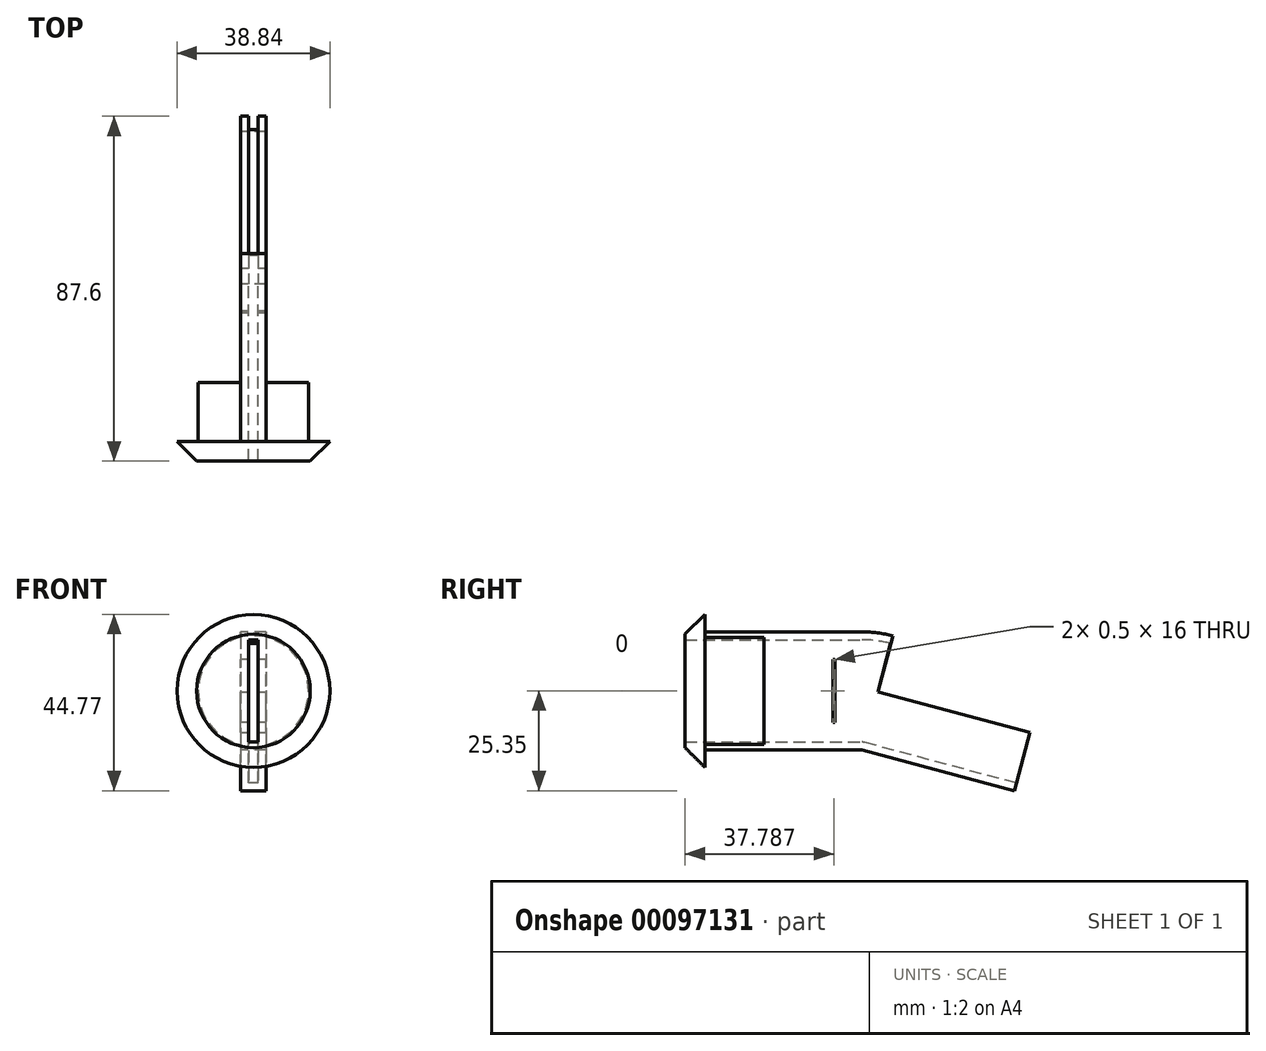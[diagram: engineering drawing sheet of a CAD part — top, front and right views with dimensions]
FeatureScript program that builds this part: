
annotation { "Feature Type Name" : "Feature", "Feature Type Description" : "" }
export const myFeature = defineFeature(function(context is Context, id is Id, definition is map)
    precondition{}
    {
        {
            var Q0;
            Q0=qCreatedBy(makeId("Front.planeOp"),FACE);
            var sketch = newSketch(context, id + "F0", { "sketchPlane" : qUnion([Q0])});
            skCircle(sketch, "E0", {"center": v(0, 0) * mm, "radius": 19.42 * mm});
            skCircle(sketch, "E1", {"center": v(0, 0) * mm, "radius": 14 * mm});
            skLineSegment(sketch, "E2.bottom", {"start": v(1.25, 13) * mm, "end": v(-1.25, 13) * mm});
            skLineSegment(sketch, "E2.top", {"start": v(1.25, -13) * mm, "end": v(-1.25, -13) * mm});
            skLineSegment(sketch, "E2.left", {"start": v(1.25, 13) * mm, "end": v(1.25, -13) * mm});
            skLineSegment(sketch, "E2.right", {"start": v(-1.25, 13) * mm, "end": v(-1.25, -13) * mm});
            skLineSegment(sketch, "E3.0", {"start": v(-3.25, 15) * mm, "end": v(-3.25, -15) * mm});
            skLineSegment(sketch, "E3.1", {"start": v(3.25, 15) * mm, "end": v(-3.25, 15) * mm});
            skLineSegment(sketch, "E3.2", {"start": v(3.25, 15) * mm, "end": v(3.25, -15) * mm});
            skLineSegment(sketch, "E3.3", {"start": v(3.25, -15) * mm, "end": v(-3.25, -15) * mm});
            skSolve(sketch);
        }
        {
            var Q0;
            {var subQ0=sQuery(id+"F0.wireOp",EDGE,"E3.0");var subQ1=sQuery(id+"F0.wireOp",EDGE,"E1");var subQ2=makeQuery(id+"F0.imprint","INTERSECT",VERTEX,{"disambiguationData":[OD(0.0)],"derivedFrom":[subQ1,subQ0]});Q0=makeQuery(id+"F0.imprint","IMPRINT",FACE,{"disambiguationData":[TD([[makeQuery(id+"F0.imprint","IMPRINT",EDGE,{"disambiguationData":[TD([[subQ2,-1.0]])],"derivedFrom":subQ1}),1.0]])]});}
            var Q1;
            Q1=makeQuery(id+"F0.imprint","IMPRINT",FACE,{"disambiguationData":[TD([[makeQuery(id+"F0.imprint","IMPRINT",EDGE,{"derivedFrom":sQuery(id+"F0.wireOp",EDGE,"E0")}),1.0]])]});
            var Q2;
            {var subQ0=sQuery(id+"F0.wireOp",EDGE,"E3.2");var subQ1=sQuery(id+"F0.wireOp",EDGE,"E1");var subQ2=makeQuery(id+"F0.imprint","INTERSECT",VERTEX,{"disambiguationData":[OD(0.0)],"derivedFrom":[subQ1,subQ0]});Q2=makeQuery(id+"F0.imprint","IMPRINT",FACE,{"disambiguationData":[TD([[makeQuery(id+"F0.imprint","IMPRINT",EDGE,{"disambiguationData":[TD([[subQ2,1.0]])],"derivedFrom":subQ1}),1.0]])]});}
            var Q3;
            Q3=makeQuery(id+"F0.imprint","IMPRINT",FACE,{"disambiguationData":[TD([[makeQuery(id+"F0.imprint","IMPRINT",EDGE,{"derivedFrom":sQuery(id+"F0.wireOp",EDGE,"E2.bottom")}),-1.0]])]});
            var Q4;
            {var subQ5=sQuery(id+"F0.wireOp",EDGE,"E3.3");Q4=makeQuery(id+"F0.imprint","IMPRINT",FACE,{"disambiguationData":[TD([[makeQuery(id+"F0.imprint","IMPRINT",EDGE,{"derivedFrom":subQ5}),-1.0]])]});}
            var Q5;
            {var subQ5=sQuery(id+"F0.wireOp",EDGE,"E3.1");Q5=makeQuery(id+"F0.imprint","IMPRINT",FACE,{"disambiguationData":[TD([[makeQuery(id+"F0.imprint","IMPRINT",EDGE,{"derivedFrom":subQ5}),1.0]])]});}
            extrude(context, id + "F1", {"entities" : qUnion([Q0, Q1, Q2, Q3, Q4, Q5]), "depth" : 5 * mm});
        }
        {
            var Q0;
            Q0=makeQuery(id+"F1.opExtrude","CAP_EDGE",EDGE,{"disambiguationData":[OSD([sQuery(id+"F0.wireOp",EDGE,"E0")])],"isStart":false});
            chamfer(context, id + "F2", {"entities" : qUnion([Q0]), "width" : 5 * mm, "tangentPropagation" : true});
        }
        {
            var Q0;
            {var subQ5=sQuery(id+"F0.wireOp",EDGE,"E3.1");Q0=makeQuery(id+"F0.imprint","IMPRINT",FACE,{"disambiguationData":[TD([[makeQuery(id+"F0.imprint","IMPRINT",EDGE,{"derivedFrom":subQ5}),1.0]])]});}
            var Q1;
            Q1=makeQuery(id+"F0.imprint","IMPRINT",FACE,{"disambiguationData":[TD([[makeQuery(id+"F0.imprint","IMPRINT",EDGE,{"derivedFrom":sQuery(id+"F0.wireOp",EDGE,"E2.bottom")}),-1.0]])]});
            var Q2;
            {var subQ5=sQuery(id+"F0.wireOp",EDGE,"E3.3");Q2=makeQuery(id+"F0.imprint","IMPRINT",FACE,{"disambiguationData":[TD([[makeQuery(id+"F0.imprint","IMPRINT",EDGE,{"derivedFrom":subQ5}),-1.0]])]});}
            extrude(context, id + "F3", {"entities" : qUnion([Q0, Q1, Q2]), "operationType" : NewBodyOperationType.ADD, "oppositeDirection" : true, "depth" : 40 * mm});
        }
        {
            var Q0;
            Q0=makeQuery(id+"F3.opExtrude","CAP_FACE",FACE,{"disambiguationData":[OSD([sQuery(id+"F0.wireOp",EDGE,"E2.bottom"),sQuery(id+"F0.wireOp",EDGE,"E2.top"),sQuery(id+"F0.wireOp",EDGE,"E2.left"),sQuery(id+"F0.wireOp",EDGE,"E2.right"),sQuery(id+"F0.wireOp",EDGE,"E3.0"),sQuery(id+"F0.wireOp",EDGE,"E3.1"),sQuery(id+"F0.wireOp",EDGE,"E3.2"),sQuery(id+"F0.wireOp",EDGE,"E3.3")])],"isStart":false});
            var Q1;
            Q1=makeQuery(id+"F3.opExtrude","CAP_EDGE",EDGE,{"disambiguationData":[OSD([sQuery(id+"F0.wireOp",EDGE,"E3.3")])],"isStart":false});
            revolve(context, id + "F4", {"operationType" : NewBodyOperationType.ADD, "entities" : qUnion([Q0]), "axis" : qUnion([Q1]), "revolveType" : RevolveType.ONE_DIRECTION, "angle" : 15 * degree});
        }
        {
            var Q0;
            Q0=makeQuery(id+"F4.opRevolve","CAP_FACE",FACE,{"disambiguationData":[OSD([sQuery(id+"F0.wireOp",EDGE,"E2.bottom"),sQuery(id+"F0.wireOp",EDGE,"E2.top"),sQuery(id+"F0.wireOp",EDGE,"E2.left"),sQuery(id+"F0.wireOp",EDGE,"E2.right"),sQuery(id+"F0.wireOp",EDGE,"E3.0"),sQuery(id+"F0.wireOp",EDGE,"E3.1"),sQuery(id+"F0.wireOp",EDGE,"E3.2"),sQuery(id+"F0.wireOp",EDGE,"E3.3")])],"isStart":false});
            var sketch = newSketch(context, id + "F5", { "sketchPlane" : qUnion([Q0])});
            skLineSegment(sketch, "E4", {"start": v(3.25, 11.18) * mm, "end": v(-3.25, 11.18) * mm});
            skSolve(sketch);
        }
        {
            var Q0;
            {var subQ2=makeQuery(id+"F4.opRevolve","CAP_EDGE",EDGE,{"disambiguationData":[OSD([sQuery(id+"F0.wireOp",EDGE,"E2.top")])],"isStart":false});Q0=makeQuery(id+"F5.imprint","IMPRINT",FACE,{"disambiguationData":[TD([[makeQuery(id+"F5.imprint","IMPRINT",EDGE,{"derivedFrom":subQ2}),-1.0]])]});}
            extrude(context, id + "F6", {"entities" : qUnion([Q0]), "operationType" : NewBodyOperationType.ADD, "depth" : 40 * mm});
        }
        {
            var Q0;
            {var subQ0=sQuery(id+"F0.wireOp",EDGE,"E3.0");Q0=makeQuery(id+"F6.boolean.opBoolean","MERGE",FACE,{"derivedFrom":[makeQuery(id+"F4.boolean.opBoolean","MERGE",FACE,{"derivedFrom":[makeQuery(id+"F3.opExtrude","SWEPT_FACE",FACE,{"disambiguationData":[OSD([subQ0])]}),makeQuery(id+"F4.opRevolve","SWEPT_FACE",FACE,{"disambiguationData":[OSD([subQ0])]})]}),makeQuery(id+"F6.opExtrude","SWEPT_FACE",FACE,{"disambiguationData":[OSD([subQ0])]})]});}
            var sketch = newSketch(context, id + "F7", { "sketchPlane" : qUnion([Q0])});
            skLineSegment(sketch, "E5.bottom", {"start": v(-33.04, -8) * mm, "end": v(-32.54, -8) * mm});
            skLineSegment(sketch, "E5.top", {"start": v(-33.04, 8) * mm, "end": v(-32.54, 8) * mm});
            skLineSegment(sketch, "E5.left", {"start": v(-33.04, -8) * mm, "end": v(-33.04, 8) * mm});
            skLineSegment(sketch, "E5.right", {"start": v(-32.54, -8) * mm, "end": v(-32.54, 8) * mm});
            skPoint(sketch, "E5.middle", {"position": v(-32.79, 0) * mm});
            skSolve(sketch);
        }
        {
            var Q0;
            Q0=makeQuery(id+"F7.imprint","IMPRINT",FACE,{"disambiguationData":[TD([[makeQuery(id+"F7.imprint","IMPRINT",EDGE,{"derivedFrom":sQuery(id+"F7.wireOp",EDGE,"E5.bottom")}),1.0]])]});
            extrude(context, id + "F8", {"entities" : qUnion([Q0]), "operationType" : NewBodyOperationType.REMOVE, "oppositeDirection" : true, "depth" : 25 * mm});
        }
        {
            var Q0;
            {var subQ0=sQuery(id+"F0.wireOp",EDGE,"E3.2");var subQ1=sQuery(id+"F0.wireOp",EDGE,"E1");var subQ2=makeQuery(id+"F0.imprint","INTERSECT",VERTEX,{"disambiguationData":[OD(0.0)],"derivedFrom":[subQ1,subQ0]});Q0=makeQuery(id+"F0.imprint","IMPRINT",FACE,{"disambiguationData":[TD([[makeQuery(id+"F0.imprint","IMPRINT",EDGE,{"disambiguationData":[TD([[subQ2,1.0]])],"derivedFrom":subQ1}),1.0]])]});}
            var Q1;
            {var subQ0=sQuery(id+"F0.wireOp",EDGE,"E3.0");var subQ1=sQuery(id+"F0.wireOp",EDGE,"E1");var subQ2=makeQuery(id+"F0.imprint","INTERSECT",VERTEX,{"disambiguationData":[OD(0.0)],"derivedFrom":[subQ1,subQ0]});Q1=makeQuery(id+"F0.imprint","IMPRINT",FACE,{"disambiguationData":[TD([[makeQuery(id+"F0.imprint","IMPRINT",EDGE,{"disambiguationData":[TD([[subQ2,-1.0]])],"derivedFrom":subQ1}),1.0]])]});}
            extrude(context, id + "F9", {"entities" : qUnion([Q0, Q1]), "operationType" : NewBodyOperationType.ADD, "oppositeDirection" : true, "depth" : 15 * mm});
        }
    });
